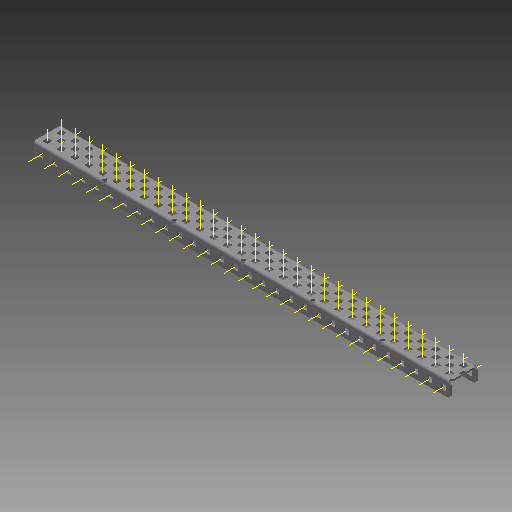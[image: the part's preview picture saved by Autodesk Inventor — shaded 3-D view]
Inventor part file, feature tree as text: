
AUTODESK INVENTOR PART (.ipt)
format: ipt  version: 2017 (Build 210142000, 142)  size: 2,193,408 bytes
history: native  units: in
note: dims shown in document units (in); Inventor stores cm internally (conversion verified against a paired STEP export)
features: other x156, pattern_linear x3, sheet_metal_op x1, extrude x1, imported_body x1, sketch x1
ambient origin geometry x8: Origin, YZ Plane, XZ Plane, XY Plane, X Axis, Y Axis, Z Axis, Center Point
bodies: Body1 (feature_tree)
feature tree (163):
  sheet_metal_op  "Fold1"
  other  "C-Channel"
  extrude  "length cut"  Depth=0.5in
  other  "top axis"
  other  "inner axis"
  other  "front axis"
  other  "back axis"
  pattern_linear  "top axes"  Spacing1=0.5in  [1 undecoded]
  pattern_linear  "inner axes"  Spacing1=0.5in  [1 undecoded]
  pattern_linear  "horiz axes"  Spacing1=-15.0in  [1 undecoded]
  other  "right plane"
  imported_body  "Base1"
  sketch  "Sketch1"  dims[d1=0.0in d4=0.5in d5=0.7874in d7=0.5in d10=0.5in d13=0.5in d14=-15.0in d15=0.0in d16=0.0in d17=0.0in d18=0.0in d19=0.0in]
  other  "Work Point1"
  other  "Work Point2"
  other  "Work Point3"
  other  "Work Point4"
  other  "Work Axis5"
  other  "Work Axis6"
  other  "Work Axis7"
  other  "Work Axis8"
  other  "Work Axis11"
  other  "Work Axis12"
  other  "Work Axis13"
  other  "Work Axis14"
  other  "Work Axis15"
  other  "Work Axis18"
  other  "Work Axis19"
  other  "Work Axis20"
  other  "Work Axis23"
  other  "Work Axis24"
  other  "Work Axis25"
  other  "Work Axis26"
  other  "Work Axis30"
  other  "Work Axis31"
  other  "Work Axis32"
  other  "Work Axis33"
  other  "left plane"
  other  "Work Axis37"
  other  "Work Axis38"
  other  "Work Axis39"
  other  "Work Axis40"
  other  "Work Axis41"
  other  "Work Axis42"
  other  "Work Axis43"
  other  "Work Axis44"
  other  "Work Axis45"
  other  "Work Axis46"
  other  "Work Axis47"
  other  "Work Axis48"
  other  "Work Axis49"
  other  "Work Axis50"
  other  "Work Axis51"
  other  "Work Axis52"
  other  "Work Axis53"
  other  "Work Axis54"
  other  "Work Axis55"
  other  "Work Axis56"
  other  "Work Axis57"
  other  "Work Axis58"
  other  "Work Axis59"
  other  "Work Axis60"
  other  "Work Axis61"
  other  "Work Axis62"
  other  "Work Axis63"
  other  "Work Axis64"
  other  "Work Axis65"
  other  "Work Axis66"
  other  "Work Axis67"
  other  "Work Axis68"
  other  "Work Axis69"
  other  "Work Axis70"
  other  "Work Axis71"
  other  "Work Axis72"
  other  "Work Axis73"
  other  "Work Axis74"
  other  "Work Axis75"
  other  "Work Axis76"
  other  "Work Axis77"
  other  "Work Axis78"
  other  "Work Axis79"
  other  "Work Axis80"
  other  "Work Axis81"
  other  "Work Axis82"
  other  "Work Axis83"
  other  "Work Axis84"
  other  "Work Axis85"
  other  "Work Axis86"
  other  "Work Axis87"
  other  "Work Axis88"
  other  "Work Axis89"
  other  "Work Axis90"
  other  "Work Axis91"
  other  "Work Axis92"
  other  "Work Axis93"
  other  "Work Axis94"
  other  "Work Axis95"
  other  "Work Axis96"
  other  "Work Axis97"
  other  "Work Axis98"
  other  "Work Axis99"
  other  "Work Axis100"
  other  "Work Axis101"
  other  "Work Axis102"
  other  "Work Axis103"
  other  "Work Axis104"
  other  "Work Axis105"
  other  "Work Axis106"
  other  "Work Axis107"
  other  "Work Axis108"
  other  "Work Axis109"
  other  "Work Axis110"
  other  "Work Axis111"
  other  "Work Axis112"
  other  "Work Axis113"
  other  "Work Axis114"
  other  "Work Axis115"
  other  "Work Axis116"
  other  "Work Axis117"
  other  "Work Axis118"
  other  "Work Axis119"
  other  "Work Axis120"
  other  "Work Axis121"
  other  "Work Axis122"
  other  "Work Axis123"
  other  "Work Axis124"
  other  "Work Axis125"
  other  "Work Axis126"
  other  "Work Axis127"
  other  "Work Axis128"
  other  "Work Axis129"
  other  "Work Axis130"
  other  "Work Axis131"
  other  "Work Axis132"
  other  "Work Axis133"
  other  "Work Axis134"
  other  "Work Axis135"
  other  "Work Axis136"
  other  "Work Axis137"
  other  "Work Axis138"
  other  "Work Axis139"
  other  "Work Axis140"
  other  "Work Axis141"
  other  "Work Axis142"
  other  "Work Axis143"
  other  "Work Axis144"
  other  "Work Axis145"
  other  "Work Axis146"
  other  "Work Axis147"
  other  "Work Axis148"
  other  "Work Axis149"
  other  "Work Axis150"
  other  "Work Axis151"
  other  "Work Axis152"
  other  "Work Axis153"
  other  "Work Axis154"
  other  "Work Axis155"
  other  "Work Axis156"
  other  "Work Axis157"
  other  "Work Axis158"
  other  "Work Axis159"
  other  "Work Axis160"
  other  "Work Axis161"
note: 3 required parameter values undecoded (feature->parameter linkage not recoverable at this tier; creation-order binding heuristic only, values carry confidence <= 0.55)
